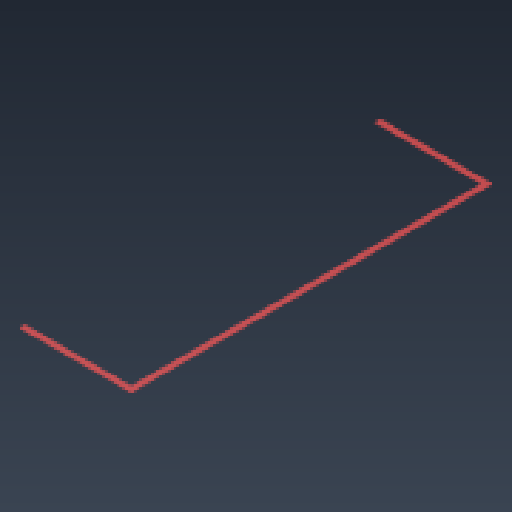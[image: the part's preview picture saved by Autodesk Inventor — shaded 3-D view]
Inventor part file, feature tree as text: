
AUTODESK INVENTOR PART (.ipt)
format: ipt  version: 2024.3 (Build 283343000, 343)  size: 83,456 bytes
history: native  units: in
note: dims shown in document units (in); Inventor stores cm internally (conversion verified against a paired STEP export)
features: extrude x1
ambient origin geometry x8: Origin, YZ Plane, XZ Plane, XY Plane, X Axis, Y Axis, Z Axis, Center Point
bodies: Solid1 (feature_tree)
feature tree (1):
  extrude  "Extrude-Thin1"  [1 undecoded]
note: 1 required parameter value undecoded (feature->parameter linkage not recoverable at this tier; creation-order binding heuristic only, values carry confidence <= 0.55)
